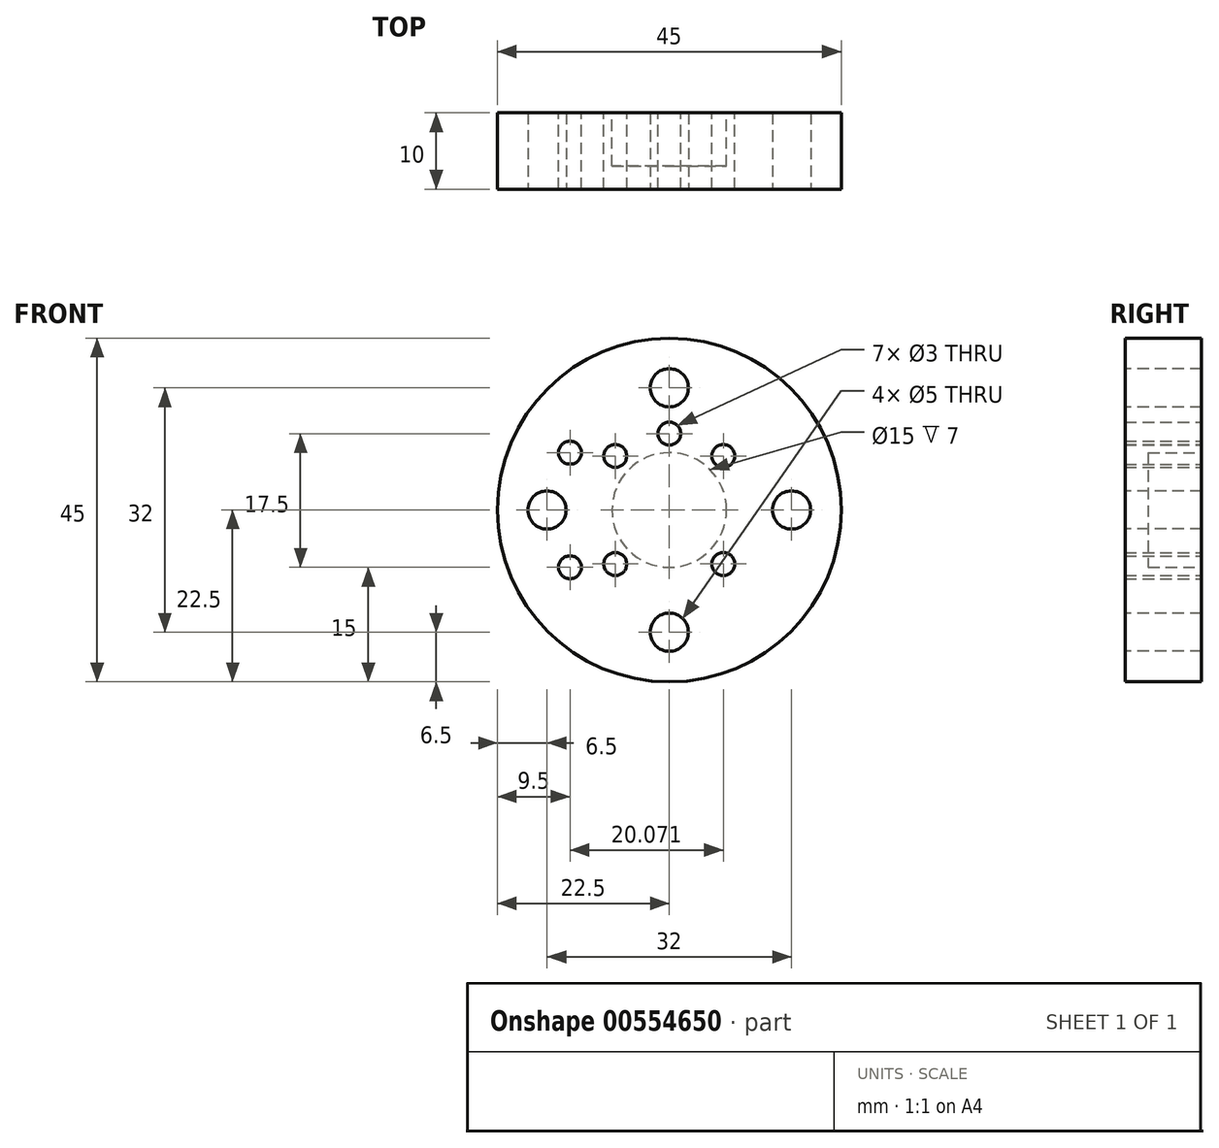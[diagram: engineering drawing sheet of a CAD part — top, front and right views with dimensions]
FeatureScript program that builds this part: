
annotation { "Feature Type Name" : "Feature", "Feature Type Description" : "" }
export const myFeature = defineFeature(function(context is Context, id is Id, definition is map)
    precondition{}
    {
        {
            var Q0;
            Q0=qCreatedBy(makeId("Front.planeOp"),FACE);
            var sketch = newSketch(context, id + "F0", { "sketchPlane" : qUnion([Q0])});
            skCircle(sketch, "E0", {"center": v(0, 0) * mm, "radius": 22.5 * mm});
            skCircle(sketch, "E1", {"center": v(-7.07, 7.07) * mm, "radius": 1.5 * mm});
            skCircle(sketch, "E2", {"center": v(7.07, 7.07) * mm, "radius": 1.5 * mm});
            skCircle(sketch, "E3", {"center": v(-7.07, -7.07) * mm, "radius": 1.5 * mm});
            skCircle(sketch, "E4", {"center": v(7.07, -7.07) * mm, "radius": 1.5 * mm});
            skCircle(sketch, "E5", {"center": v(-13, 7.5) * mm, "radius": 1.5 * mm});
            skCircle(sketch, "E6", {"center": v(-13, -7.5) * mm, "radius": 1.5 * mm});
            skCircle(sketch, "E7", {"center": v(0, 10) * mm, "radius": 1.5 * mm});
            skSolve(sketch);
        }
        {
            var Q0;
            Q0=makeQuery(id+"F0.imprint","IMPRINT",FACE,{"disambiguationData":[TD([[makeQuery(id+"F0.imprint","IMPRINT",EDGE,{"derivedFrom":sQuery(id+"F0.wireOp",EDGE,"E0")}),1.0]])]});
            extrude(context, id + "F1", {"entities" : qUnion([Q0]), "depth" : 10 * mm, "offsetDistance" : 25 * mm});
        }
        {
            var Q0;
            Q0=makeQuery(id+"F1.opExtrude","CAP_FACE",FACE,{"disambiguationData":[OSD([sQuery(id+"F0.wireOp",EDGE,"E0"),sQuery(id+"F0.wireOp",EDGE,"E1"),sQuery(id+"F0.wireOp",EDGE,"E2"),sQuery(id+"F0.wireOp",EDGE,"E3"),sQuery(id+"F0.wireOp",EDGE,"E4"),sQuery(id+"F0.wireOp",EDGE,"E5"),sQuery(id+"F0.wireOp",EDGE,"E6"),sQuery(id+"F0.wireOp",EDGE,"E7")])],"isStart":true});
            var sketch = newSketch(context, id + "F2", { "sketchPlane" : qUnion([Q0])});
            skCircle(sketch, "E8", {"center": v(0, 0) * mm, "radius": 7.5 * mm});
            skSolve(sketch);
        }
        {
            var Q0;
            Q0=makeQuery(id+"F2.imprint","IMPRINT",FACE,{"disambiguationData":[TD([[makeQuery(id+"F2.imprint","IMPRINT",EDGE,{"derivedFrom":sQuery(id+"F2.wireOp",EDGE,"E8")}),1.0]])]});
            extrude(context, id + "F3", {"entities" : qUnion([Q0]), "operationType" : NewBodyOperationType.REMOVE, "oppositeDirection" : true, "depth" : 7 * mm, "offsetDistance" : 25 * mm});
        }
        {
            var Q0;
            Q0=makeQuery(id+"F1.opExtrude","CAP_FACE",FACE,{"disambiguationData":[OSD([sQuery(id+"F0.wireOp",EDGE,"E0"),sQuery(id+"F0.wireOp",EDGE,"E1"),sQuery(id+"F0.wireOp",EDGE,"E2"),sQuery(id+"F0.wireOp",EDGE,"E3"),sQuery(id+"F0.wireOp",EDGE,"E4"),sQuery(id+"F0.wireOp",EDGE,"E5"),sQuery(id+"F0.wireOp",EDGE,"E6"),sQuery(id+"F0.wireOp",EDGE,"E7")])],"isStart":false});
            var sketch = newSketch(context, id + "F4", { "sketchPlane" : qUnion([Q0])});
            skCircle(sketch, "E9", {"center": v(0, 16) * mm, "radius": 2.5 * mm});
            skCircle(sketch, "E10", {"center": v(0, -16) * mm, "radius": 2.5 * mm});
            skCircle(sketch, "E11", {"center": v(16, 0) * mm, "radius": 2.5 * mm});
            skCircle(sketch, "E12", {"center": v(-16, 0) * mm, "radius": 2.5 * mm});
            skSolve(sketch);
        }
        {
            var Q0;
            Q0=makeQuery(id+"F4.imprint","IMPRINT",FACE,{"disambiguationData":[TD([[makeQuery(id+"F4.imprint","IMPRINT",EDGE,{"derivedFrom":sQuery(id+"F4.wireOp",EDGE,"E9")}),1.0]])]});
            var Q1;
            Q1=makeQuery(id+"F4.imprint","IMPRINT",FACE,{"disambiguationData":[TD([[makeQuery(id+"F4.imprint","IMPRINT",EDGE,{"derivedFrom":sQuery(id+"F4.wireOp",EDGE,"E11")}),1.0]])]});
            var Q2;
            Q2=makeQuery(id+"F4.imprint","IMPRINT",FACE,{"disambiguationData":[TD([[makeQuery(id+"F4.imprint","IMPRINT",EDGE,{"derivedFrom":sQuery(id+"F4.wireOp",EDGE,"E10")}),1.0]])]});
            var Q3;
            Q3=makeQuery(id+"F4.imprint","IMPRINT",FACE,{"disambiguationData":[TD([[makeQuery(id+"F4.imprint","IMPRINT",EDGE,{"derivedFrom":sQuery(id+"F4.wireOp",EDGE,"E12")}),1.0]])]});
            extrude(context, id + "F5", {"entities" : qUnion([Q0, Q1, Q2, Q3]), "operationType" : NewBodyOperationType.REMOVE, "oppositeDirection" : true, "depth" : 25 * mm, "offsetDistance" : 25 * mm});
        }
    });
